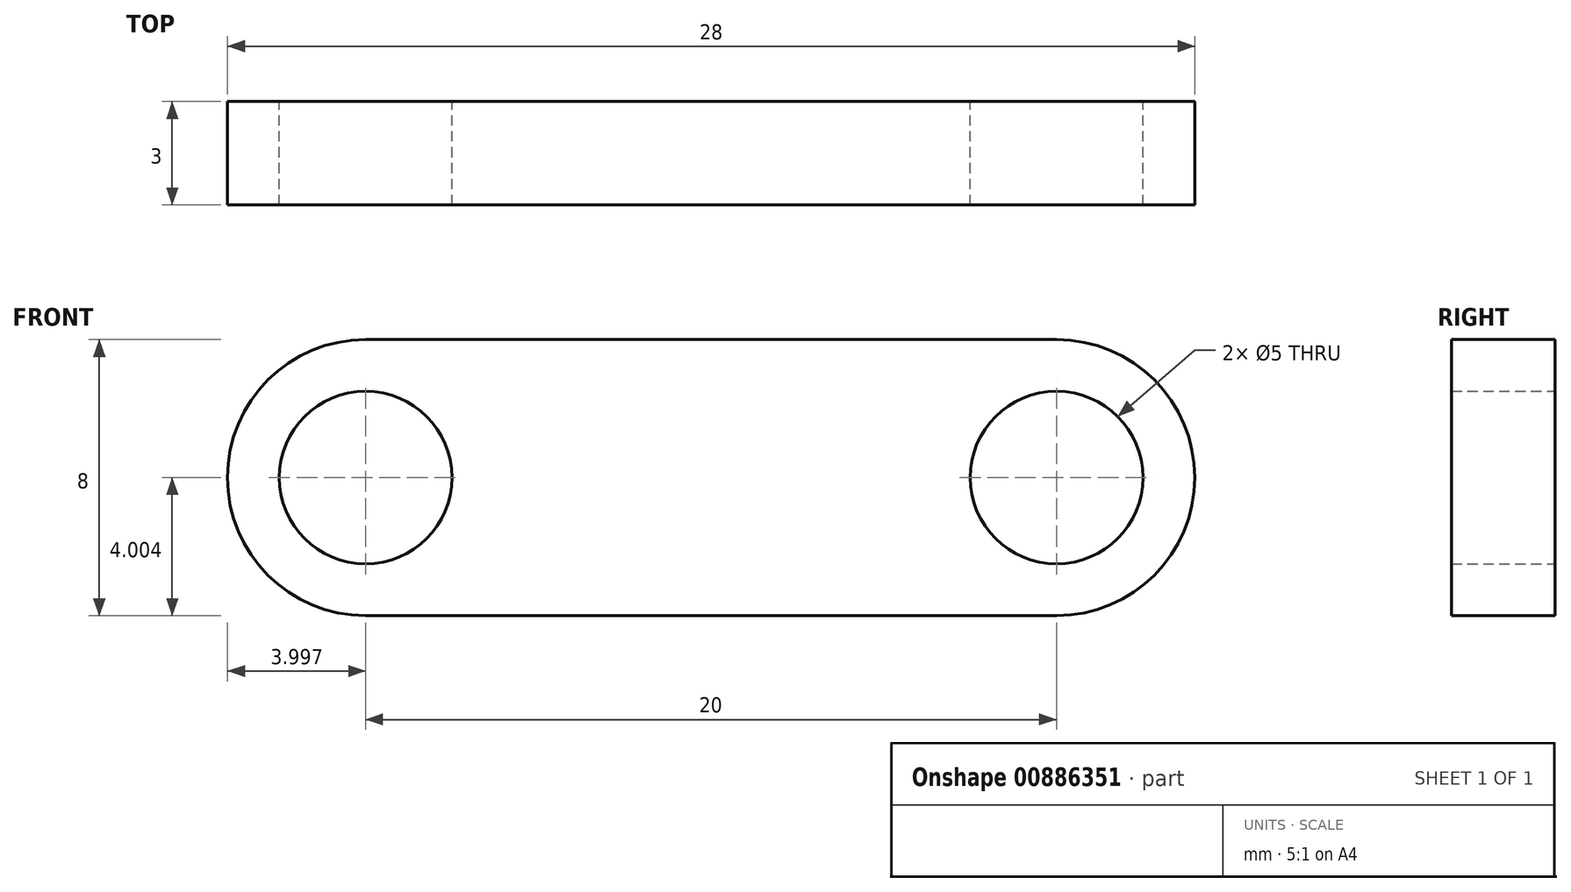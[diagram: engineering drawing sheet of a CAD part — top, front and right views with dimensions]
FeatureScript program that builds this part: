
annotation { "Feature Type Name" : "Feature", "Feature Type Description" : "" }
export const myFeature = defineFeature(function(context is Context, id is Id, definition is map)
    precondition{}
    {
        {
            var Q0;
            Q0=qCreatedBy(makeId("Front.planeOp"),FACE);
            var sketch = newSketch(context, id + "F0", { "sketchPlane" : qUnion([Q0])});
            skLineSegment(sketch, "E0.bottom", {"start": v(-12.41, 15.7) * mm, "end": v(7.59, 15.7) * mm});
            skLineSegment(sketch, "E0.top", {"start": v(-12.41, 7.7) * mm, "end": v(7.59, 7.7) * mm});
            skArc(sketch, "E1", {"start": v(-12.41, 15.7) * mm, "mid": v(-16.41, 11.7) * mm, "end": v(-12.41, 7.7) * mm});
            skArc(sketch, "E2", {"start": v(7.59, 7.7) * mm, "mid": v(11.59, 11.7) * mm, "end": v(7.59, 15.7) * mm});
            skCircle(sketch, "E3", {"center": v(-12.41, 11.7) * mm, "radius": 2.5 * mm});
            skCircle(sketch, "E4", {"center": v(7.59, 11.7) * mm, "radius": 2.5 * mm});
            skSolve(sketch);
        }
        {
            var Q0;
            Q0 = qSketchRegion(id + "F0", true);
            extrude(context, id + "F1", {"entities" : qUnion([Q0]), "depth" : 3 * mm, "offsetDistance" : 25 * mm});
        }
    });
